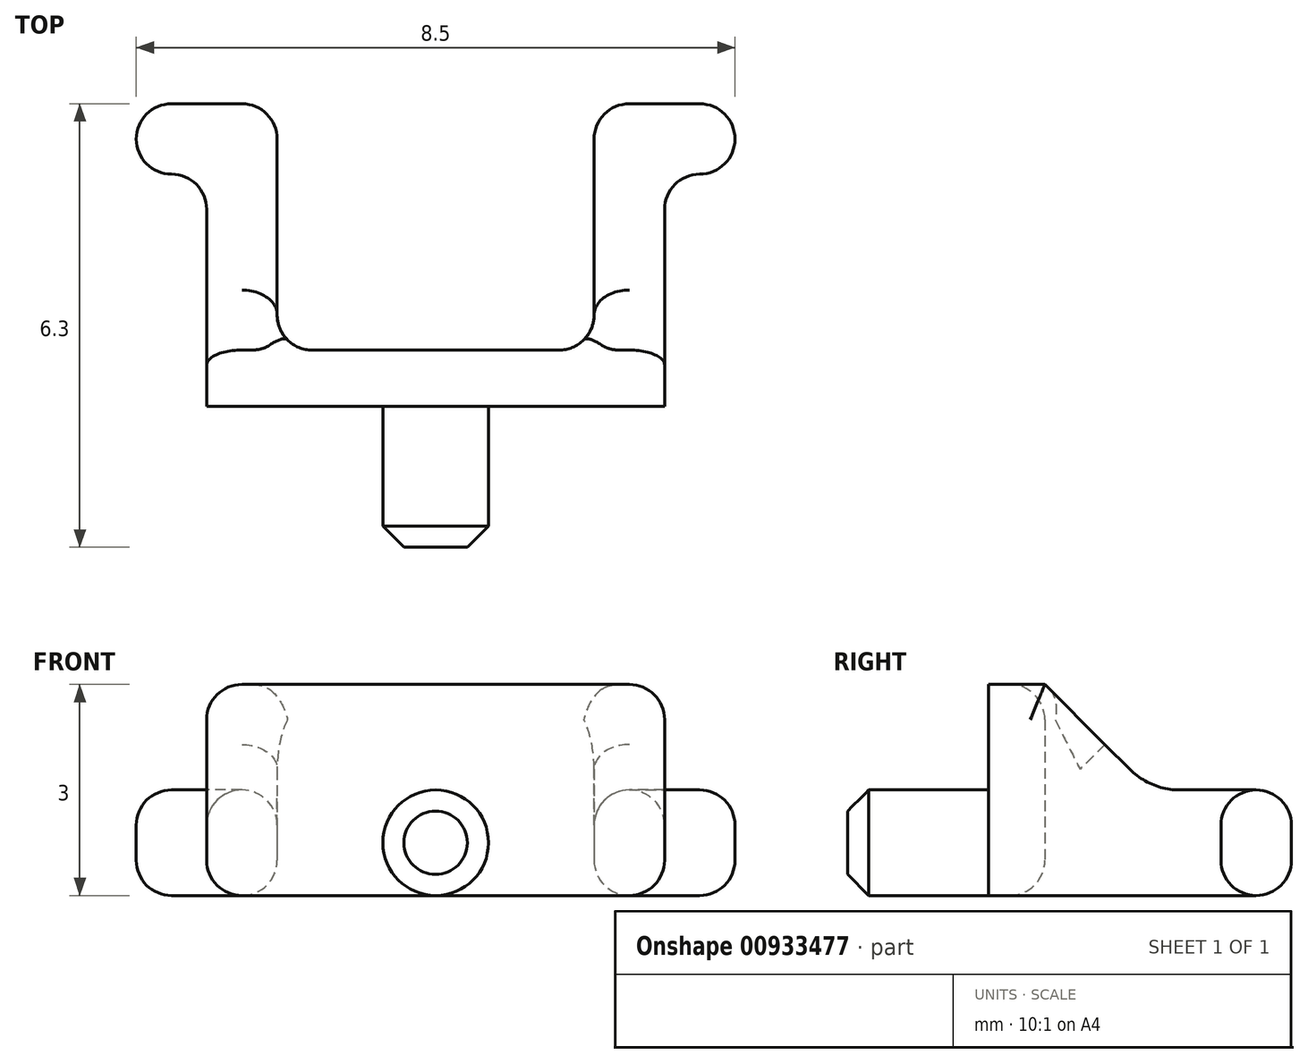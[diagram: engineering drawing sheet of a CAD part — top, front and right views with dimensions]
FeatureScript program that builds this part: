
annotation { "Feature Type Name" : "Feature", "Feature Type Description" : "" }
export const myFeature = defineFeature(function(context is Context, id is Id, definition is map)
    precondition{}
    {
        {
            var Q0;
            Q0=qCreatedBy(makeId("Top.planeOp"),FACE);
            var sketch = newSketch(context, id + "F0", { "sketchPlane" : qUnion([Q0])});
            skLineSegment(sketch, "E0", {"start": v(-3.25, 0) * mm, "end": v(-0.75, 0) * mm});
            skPoint(sketch, "E1", {"position": v(0, 0) * mm});
            skLineSegment(sketch, "E2", {"start": v(0, -3) * mm, "end": v(0, 7.11) * mm, "construction": true});
            skLineSegment(sketch, "E3", {"start": v(2.25, 1.3) * mm, "end": v(2.25, 3.8) * mm});
            skLineSegment(sketch, "E4", {"start": v(-2.25, 1.3) * mm, "end": v(-2.25, 3.8) * mm});
            skLineSegment(sketch, "E5", {"start": v(-1.75, 0.8) * mm, "end": v(1.75, 0.8) * mm});
            skPoint(sketch, "E6", {"position": v(0, 0.8) * mm});
            skLineSegment(sketch, "E7", {"start": v(-2.75, 4.3) * mm, "end": v(-3.75, 4.3) * mm});
            skLineSegment(sketch, "E8", {"start": v(2.75, 4.3) * mm, "end": v(3.75, 4.3) * mm});
            skLineSegment(sketch, "E9", {"start": v(-4.25, 3.8) * mm, "end": v(-4.25, 3.8) * mm});
            skLineSegment(sketch, "E10", {"start": v(-3.75, 3.3) * mm, "end": v(-3.75, 3.3) * mm});
            skLineSegment(sketch, "E11", {"start": v(-3.25, 2.8) * mm, "end": v(-3.25, 0) * mm});
            skLineSegment(sketch, "E12", {"start": v(4.25, 3.8) * mm, "end": v(4.25, 3.8) * mm});
            skLineSegment(sketch, "E13", {"start": v(3.75, 3.3) * mm, "end": v(3.75, 3.3) * mm});
            skLineSegment(sketch, "E14", {"start": v(3.25, 2.8) * mm, "end": v(3.25, 0) * mm});
            skPoint(sketch, "E15.visualSharp", {"position": v(-2.25, 0.8) * mm});
            skArc(sketch, "E15.filletArc", {"start": v(-2.25, 1.3) * mm, "mid": v(-2.1, 0.95) * mm, "end": v(-1.75, 0.8) * mm});
            skPoint(sketch, "E16.visualSharp", {"position": v(2.25, 0.8) * mm});
            skArc(sketch, "E16.filletArc", {"start": v(1.75, 0.8) * mm, "mid": v(2.1, 0.95) * mm, "end": v(2.25, 1.3) * mm});
            skPoint(sketch, "E17.visualSharp", {"position": v(3.25, 0.8) * mm});
            skPoint(sketch, "E18.visualSharp", {"position": v(3.25, 3.3) * mm});
            skArc(sketch, "E18.filletArc", {"start": v(3.75, 3.3) * mm, "mid": v(3.4, 3.15) * mm, "end": v(3.25, 2.8) * mm});
            skPoint(sketch, "E19.visualSharp", {"position": v(-3.25, 0.8) * mm});
            skPoint(sketch, "E20.visualSharp", {"position": v(-3.25, 3.3) * mm});
            skArc(sketch, "E20.filletArc", {"start": v(-3.25, 2.8) * mm, "mid": v(-3.4, 3.15) * mm, "end": v(-3.75, 3.3) * mm});
            skPoint(sketch, "E21.visualSharp", {"position": v(-2.25, 4.3) * mm});
            skArc(sketch, "E21.filletArc", {"start": v(-2.25, 3.8) * mm, "mid": v(-2.4, 4.15) * mm, "end": v(-2.75, 4.3) * mm});
            skPoint(sketch, "E22.visualSharp", {"position": v(2.25, 4.3) * mm});
            skArc(sketch, "E22.filletArc", {"start": v(2.75, 4.3) * mm, "mid": v(2.4, 4.15) * mm, "end": v(2.25, 3.8) * mm});
            skPoint(sketch, "E23.visualSharp", {"position": v(4.25, 4.3) * mm});
            skArc(sketch, "E23.filletArc", {"start": v(4.25, 3.8) * mm, "mid": v(4.1, 4.15) * mm, "end": v(3.75, 4.3) * mm});
            skPoint(sketch, "E24.visualSharp", {"position": v(4.25, 3.3) * mm});
            skArc(sketch, "E24.filletArc", {"start": v(3.75, 3.3) * mm, "mid": v(4.1, 3.45) * mm, "end": v(4.25, 3.8) * mm});
            skPoint(sketch, "E25.visualSharp", {"position": v(-4.25, 4.3) * mm});
            skArc(sketch, "E25.filletArc", {"start": v(-3.75, 4.3) * mm, "mid": v(-4.1, 4.15) * mm, "end": v(-4.25, 3.8) * mm});
            skPoint(sketch, "E26.visualSharp", {"position": v(-4.25, 3.3) * mm});
            skArc(sketch, "E26.filletArc", {"start": v(-4.25, 3.8) * mm, "mid": v(-4.1, 3.45) * mm, "end": v(-3.75, 3.3) * mm});
            skLineSegment(sketch, "E27.top", {"start": v(-0.75, -2) * mm, "end": v(0.75, -2) * mm});
            skLineSegment(sketch, "E27.left", {"start": v(-0.75, 0) * mm, "end": v(-0.75, -2) * mm});
            skLineSegment(sketch, "E27.right", {"start": v(0.75, 0) * mm, "end": v(0.75, -2) * mm});
            skPoint(sketch, "E28", {"position": v(0, -2) * mm});
            skLineSegment(sketch, "E29.trimOffspring", {"start": v(0.75, 0) * mm, "end": v(3.25, 0) * mm});
            skPoint(sketch, "E30.orphan", {"position": v(-5, 0) * mm});
            skPoint(sketch, "E31.orphan", {"position": v(5, 0) * mm});
            skSolve(sketch);
        }
        {
            var Q0;
            Q0=qSketchRegion(id+"F0",true);
            extrude(context, id + "F1", {"entities" : qUnion([Q0]), "depth" : 1.5 * mm, "offsetDistance" : 25 * mm});
        }
        {
            var Q0;
            Q0=makeQuery(id+"F1.opExtrude","CAP_FACE",FACE,{"disambiguationData":[OSD([sQuery(id+"F0.wireOp",EDGE,"E0"),sQuery(id+"F0.wireOp",EDGE,"6YUp3G7D-HScl-yHn5-GseC-h8JY3a3RTnfq"),sQuery(id+"F0.wireOp",EDGE,"Xoj59s7T-2QtX-ZDX5-LiLJ-oQHR1xyVejqm"),sQuery(id+"F0.wireOp",EDGE,"Zc0sCTJD-TUej-OjTx-Aevo-d0EqPVeEhSTX"),sQuery(id+"F0.wireOp",EDGE,"E3"),sQuery(id+"F0.wireOp",EDGE,"E4"),sQuery(id+"F0.wireOp",EDGE,"fb0ed693-0343-43f7-9de8-dc647e30bef6.trimOffspring"),sQuery(id+"F0.wireOp",EDGE,"E5"),sQuery(id+"F0.wireOp",EDGE,"E7"),sQuery(id+"F0.wireOp",EDGE,"E8"),sQuery(id+"F0.wireOp",EDGE,"E15.filletArc"),sQuery(id+"F0.wireOp",EDGE,"E16.filletArc"),sQuery(id+"F0.wireOp",EDGE,"E17.filletArc"),sQuery(id+"F0.wireOp",EDGE,"E18.filletArc"),sQuery(id+"F0.wireOp",EDGE,"E19.filletArc"),sQuery(id+"F0.wireOp",EDGE,"E20.filletArc"),sQuery(id+"F0.wireOp",EDGE,"E21.filletArc"),sQuery(id+"F0.wireOp",EDGE,"E22.filletArc"),sQuery(id+"F0.wireOp",EDGE,"E23.filletArc"),sQuery(id+"F0.wireOp",EDGE,"E24.filletArc"),sQuery(id+"F0.wireOp",EDGE,"E25.filletArc"),sQuery(id+"F0.wireOp",EDGE,"E26.filletArc")])],"isStart":false});
            var sketch = newSketch(context, id + "F2", { "sketchPlane" : qUnion([Q0])});
            skLineSegment(sketch, "E32.0", {"start": v(-3.25, 0) * mm, "end": v(-3.25, 0) * mm});
            skLineSegment(sketch, "E33.0", {"start": v(-3.25, 0) * mm, "end": v(-3.25, 0.8) * mm});
            skLineSegment(sketch, "E34.0", {"start": v(3.25, 0.8) * mm, "end": v(3.25, 0) * mm});
            skLineSegment(sketch, "E35", {"start": v(-3.25, 0.8) * mm, "end": v(3.25, 0.8) * mm});
            skLineSegment(sketch, "E36.0", {"start": v(-3.25, 0) * mm, "end": v(3.25, 0) * mm});
            skPoint(sketch, "E37.orphan", {"position": v(-0.75, 0) * mm});
            skSolve(sketch);
        }
        {
            var Q0;
            Q0=qSketchRegion(id+"F2",true);
            extrude(context, id + "F3", {"entities" : qUnion([Q0]), "operationType" : NewBodyOperationType.ADD, "depth" : 1.5 * mm, "offsetDistance" : 25 * mm});
        }
        {
            var Q0;
            {var subQ4=sQuery(id+"F0.wireOp",EDGE,"E15.filletArc");var subQ5=sQuery(id+"F2.wireOp",EDGE,"E35");Q0=makeQuery(id+"F3.boolean.opBoolean","SPLIT",EDGE,{"disambiguationData":[TD([makeQuery(id+"F1.opExtrude","SWEPT_FACE",FACE,{"disambiguationData":[OSD([subQ4])]})])],"derivedFrom":makeQuery(id+"F3.opExtrude","CAP_EDGE",EDGE,{"disambiguationData":[OSD([subQ5])],"isStart":true})});}
            var Q1;
            {var subQ3=sQuery(id+"F0.wireOp",EDGE,"E16.filletArc");var subQ5=sQuery(id+"F2.wireOp",EDGE,"E35");Q1=makeQuery(id+"F3.boolean.opBoolean","SPLIT",EDGE,{"disambiguationData":[TD([makeQuery(id+"F1.opExtrude","SWEPT_FACE",FACE,{"disambiguationData":[OSD([subQ3])]})])],"derivedFrom":makeQuery(id+"F3.opExtrude","CAP_EDGE",EDGE,{"disambiguationData":[OSD([subQ5])],"isStart":true})});}
            chamfer(context, id + "F4", {"entities" : qUnion([Q0, Q1]), "width" : 1.5 * mm, "tangentPropagation" : true});
        }
        {
            var Q0;
            {var subQ0=sQuery(id+"F2.wireOp",EDGE,"E35");var subQ1=makeQuery(id+"F3.opExtrude","SWEPT_FACE",FACE,{"disambiguationData":[OSD([subQ0])]});var subQ2=sQuery(id+"F0.wireOp",EDGE,"E5");var subQ3=makeQuery(id+"F1.opExtrude","SWEPT_FACE",FACE,{"disambiguationData":[OSD([subQ2])]});var subQ4=sQuery(id+"F0.wireOp",EDGE,"fb0ed693-0343-43f7-9de8-dc647e30bef6.trimOffspring");var subQ5=makeQuery(id+"F1.opExtrude","SWEPT_FACE",FACE,{"disambiguationData":[OSD([subQ4])]});var subQ6=sQuery(id+"F0.wireOp",EDGE,"Xoj59s7T-2QtX-ZDX5-LiLJ-oQHR1xyVejqm");var subQ7=makeQuery(id+"F1.opExtrude","SWEPT_FACE",FACE,{"disambiguationData":[OSD([subQ6])]});var subQ9=sQuery(id+"F0.wireOp",EDGE,"E15.filletArc");Q0=makeQuery(id+"F4.opChamfer","BLEND_EDGE",EDGE,{"blendedFrom":[makeQuery(id+"F3.boolean.opBoolean","SPLIT",EDGE,{"disambiguationData":[TD([makeQuery(id+"F1.opExtrude","SWEPT_FACE",FACE,{"disambiguationData":[OSD([subQ9])]})])],"derivedFrom":makeQuery(id+"F3.opExtrude","CAP_EDGE",EDGE,{"disambiguationData":[OSD([subQ0])],"isStart":true})}),makeQuery(id+"F3.boolean.opBoolean","MERGE",FACE,{"derivedFrom":[subQ7,subQ5,subQ3,subQ1]})],"blendedInto":[makeQuery(id+"F3.boolean.opBoolean","MERGE",FACE,{"derivedFrom":[subQ7,subQ5,subQ3,subQ1]})]});}
            var Q1;
            {var subQ0=sQuery(id+"F2.wireOp",EDGE,"E35");var subQ1=makeQuery(id+"F3.opExtrude","SWEPT_FACE",FACE,{"disambiguationData":[OSD([subQ0])]});var subQ2=sQuery(id+"F0.wireOp",EDGE,"E5");var subQ3=makeQuery(id+"F1.opExtrude","SWEPT_FACE",FACE,{"disambiguationData":[OSD([subQ2])]});var subQ4=sQuery(id+"F0.wireOp",EDGE,"fb0ed693-0343-43f7-9de8-dc647e30bef6.trimOffspring");var subQ5=makeQuery(id+"F1.opExtrude","SWEPT_FACE",FACE,{"disambiguationData":[OSD([subQ4])]});var subQ6=sQuery(id+"F0.wireOp",EDGE,"Xoj59s7T-2QtX-ZDX5-LiLJ-oQHR1xyVejqm");var subQ7=makeQuery(id+"F1.opExtrude","SWEPT_FACE",FACE,{"disambiguationData":[OSD([subQ6])]});var subQ8=sQuery(id+"F0.wireOp",EDGE,"E16.filletArc");Q1=makeQuery(id+"F4.opChamfer","BLEND_EDGE",EDGE,{"blendedFrom":[makeQuery(id+"F3.boolean.opBoolean","SPLIT",EDGE,{"disambiguationData":[TD([makeQuery(id+"F1.opExtrude","SWEPT_FACE",FACE,{"disambiguationData":[OSD([subQ8])]})])],"derivedFrom":makeQuery(id+"F3.opExtrude","CAP_EDGE",EDGE,{"disambiguationData":[OSD([subQ0])],"isStart":true})}),makeQuery(id+"F3.boolean.opBoolean","MERGE",FACE,{"derivedFrom":[subQ7,subQ5,subQ3,subQ1]})],"blendedInto":[makeQuery(id+"F3.boolean.opBoolean","MERGE",FACE,{"derivedFrom":[subQ7,subQ5,subQ3,subQ1]})]});}
            var Q2;
            {var subQ0=sQuery(id+"F0.wireOp",EDGE,"E22.filletArc");var subQ1=sQuery(id+"F0.wireOp",EDGE,"E17.filletArc");var subQ3=sQuery(id+"F0.wireOp",EDGE,"E14");var subQ4=sQuery(id+"F0.wireOp",EDGE,"E8");var subQ5=sQuery(id+"F0.wireOp",EDGE,"E16.filletArc");var subQ6=makeQuery(id+"F1.opExtrude","SWEPT_FACE",FACE,{"disambiguationData":[OSD([subQ5])]});var subQ7=sQuery(id+"F0.wireOp",EDGE,"Xoj59s7T-2QtX-ZDX5-LiLJ-oQHR1xyVejqm");var subQ9=sQuery(id+"F0.wireOp",EDGE,"E5");var subQ11=sQuery(id+"F2.wireOp",EDGE,"E35");var subQ13=sQuery(id+"F0.wireOp",EDGE,"E18.filletArc");var subQ14=sQuery(id+"F0.wireOp",EDGE,"E3");var subQ15=sQuery(id+"F0.wireOp",EDGE,"fb0ed693-0343-43f7-9de8-dc647e30bef6.trimOffspring");var subQ17=sQuery(id+"F0.wireOp",EDGE,"E24.filletArc");var subQ18=sQuery(id+"F0.wireOp",EDGE,"E23.filletArc");var subQ19=makeQuery(id+"F1.opExtrude","CAP_FACE",FACE,{"disambiguationData":[OSD([sQuery(id+"F0.wireOp",EDGE,"E0"),sQuery(id+"F0.wireOp",EDGE,"6YUp3G7D-HScl-yHn5-GseC-h8JY3a3RTnfq"),subQ7,sQuery(id+"F0.wireOp",EDGE,"Zc0sCTJD-TUej-OjTx-Aevo-d0EqPVeEhSTX"),subQ14,sQuery(id+"F0.wireOp",EDGE,"E4"),subQ15,subQ9,sQuery(id+"F0.wireOp",EDGE,"E7"),subQ4,sQuery(id+"F0.wireOp",EDGE,"E11"),subQ3,sQuery(id+"F0.wireOp",EDGE,"E15.filletArc"),subQ5,subQ1,subQ13,sQuery(id+"F0.wireOp",EDGE,"E19.filletArc"),sQuery(id+"F0.wireOp",EDGE,"E20.filletArc"),sQuery(id+"F0.wireOp",EDGE,"E21.filletArc"),subQ0,subQ18,subQ17,sQuery(id+"F0.wireOp",EDGE,"E25.filletArc"),sQuery(id+"F0.wireOp",EDGE,"E26.filletArc")])],"isStart":false});Q2=makeQuery(id+"F4.opChamfer","BLEND_EDGE",EDGE,{"blendedFrom":[makeQuery(id+"F3.boolean.opBoolean","SPLIT",EDGE,{"disambiguationData":[TD([subQ6])],"derivedFrom":makeQuery(id+"F3.opExtrude","CAP_EDGE",EDGE,{"disambiguationData":[OSD([subQ11])],"isStart":true})}),makeQuery(id+"F3.boolean.opBoolean","SPLIT",FACE,{"disambiguationData":[TD([makeQuery(id+"F1.opExtrude","SWEPT_FACE",FACE,{"disambiguationData":[OSD([subQ14])]})])],"derivedFrom":subQ19})],"blendedInto":[makeQuery(id+"F3.boolean.opBoolean","SPLIT",FACE,{"disambiguationData":[TD([makeQuery(id+"F1.opExtrude","SWEPT_FACE",FACE,{"disambiguationData":[OSD([subQ14])]})])],"derivedFrom":subQ19})]});}
            var Q3;
            {var subQ0=sQuery(id+"F0.wireOp",EDGE,"E15.filletArc");var subQ1=makeQuery(id+"F1.opExtrude","SWEPT_FACE",FACE,{"disambiguationData":[OSD([subQ0])]});var subQ2=sQuery(id+"F0.wireOp",EDGE,"E11");var subQ3=sQuery(id+"F0.wireOp",EDGE,"E7");var subQ4=sQuery(id+"F0.wireOp",EDGE,"Xoj59s7T-2QtX-ZDX5-LiLJ-oQHR1xyVejqm");var subQ6=sQuery(id+"F0.wireOp",EDGE,"E21.filletArc");var subQ7=sQuery(id+"F0.wireOp",EDGE,"E5");var subQ9=sQuery(id+"F2.wireOp",EDGE,"E35");var subQ11=sQuery(id+"F0.wireOp",EDGE,"E19.filletArc");var subQ13=sQuery(id+"F0.wireOp",EDGE,"E4");var subQ14=sQuery(id+"F0.wireOp",EDGE,"E20.filletArc");var subQ15=sQuery(id+"F0.wireOp",EDGE,"fb0ed693-0343-43f7-9de8-dc647e30bef6.trimOffspring");var subQ17=sQuery(id+"F0.wireOp",EDGE,"E26.filletArc");var subQ18=sQuery(id+"F0.wireOp",EDGE,"E25.filletArc");var subQ19=makeQuery(id+"F1.opExtrude","CAP_FACE",FACE,{"disambiguationData":[OSD([sQuery(id+"F0.wireOp",EDGE,"E0"),sQuery(id+"F0.wireOp",EDGE,"6YUp3G7D-HScl-yHn5-GseC-h8JY3a3RTnfq"),subQ4,sQuery(id+"F0.wireOp",EDGE,"Zc0sCTJD-TUej-OjTx-Aevo-d0EqPVeEhSTX"),sQuery(id+"F0.wireOp",EDGE,"E3"),subQ13,subQ15,subQ7,subQ3,sQuery(id+"F0.wireOp",EDGE,"E8"),subQ2,sQuery(id+"F0.wireOp",EDGE,"E14"),subQ0,sQuery(id+"F0.wireOp",EDGE,"E16.filletArc"),sQuery(id+"F0.wireOp",EDGE,"E17.filletArc"),sQuery(id+"F0.wireOp",EDGE,"E18.filletArc"),subQ11,subQ14,subQ6,sQuery(id+"F0.wireOp",EDGE,"E22.filletArc"),sQuery(id+"F0.wireOp",EDGE,"E23.filletArc"),sQuery(id+"F0.wireOp",EDGE,"E24.filletArc"),subQ18,subQ17])],"isStart":false});Q3=makeQuery(id+"F4.opChamfer","BLEND_EDGE",EDGE,{"blendedFrom":[makeQuery(id+"F3.boolean.opBoolean","SPLIT",EDGE,{"disambiguationData":[TD([subQ1])],"derivedFrom":makeQuery(id+"F3.opExtrude","CAP_EDGE",EDGE,{"disambiguationData":[OSD([subQ9])],"isStart":true})}),makeQuery(id+"F3.boolean.opBoolean","SPLIT",FACE,{"disambiguationData":[TD([makeQuery(id+"F1.opExtrude","SWEPT_FACE",FACE,{"disambiguationData":[OSD([subQ13])]})])],"derivedFrom":subQ19})],"blendedInto":[makeQuery(id+"F3.boolean.opBoolean","SPLIT",FACE,{"disambiguationData":[TD([makeQuery(id+"F1.opExtrude","SWEPT_FACE",FACE,{"disambiguationData":[OSD([subQ13])]})])],"derivedFrom":subQ19})]});}
            fillet(context, id + "F5", {"entities" : qUnion([Q0, Q1, Q2, Q3]), "radius" : 1 * mm, "tangentPropagation" : true, "allowEdgeOverflow" : false});
        }
        {
            var Q0;
            Q0=makeQuery(id+"F3.opExtrude","CAP_EDGE",EDGE,{"disambiguationData":[OSD([sQuery(id+"F2.wireOp",EDGE,"E35")])],"isStart":false});
            var Q1;
            Q1=makeQuery(id+"F1.opExtrude","CAP_EDGE",EDGE,{"disambiguationData":[OSD([sQuery(id+"F0.wireOp",EDGE,"E8")])],"isStart":false});
            var Q2;
            Q2=makeQuery(id+"F1.opExtrude","CAP_EDGE",EDGE,{"disambiguationData":[OSD([sQuery(id+"F0.wireOp",EDGE,"E7")])],"isStart":false});
            var Q3;
            Q3=makeQuery(id+"F3.opExtrude","CAP_EDGE",EDGE,{"disambiguationData":[OSD([sQuery(id+"F2.wireOp",EDGE,"E34.0")])],"isStart":false});
            var Q4;
            Q4=makeQuery(id+"F3.opExtrude","CAP_EDGE",EDGE,{"disambiguationData":[OSD([sQuery(id+"F2.wireOp",EDGE,"E33.0")])],"isStart":false});
            var Q5;
            Q5=makeQuery(id+"F1.opExtrude","CAP_EDGE",EDGE,{"disambiguationData":[OSD([sQuery(id+"F0.wireOp",EDGE,"E5")])],"isStart":true});
            fillet(context, id + "F6", {"entities" : qUnion([Q0, Q1, Q2, Q3, Q4, Q5]), "radius" : 0.5 * mm, "tangentPropagation" : true, "defaultsChanged" : false, "vertexSettings" : [], "allowEdgeOverflow" : false});
        }
        {
            var Q0;
            Q0=makeQuery(id+"F1.opExtrude","CAP_EDGE",EDGE,{"disambiguationData":[OSD([sQuery(id+"F0.wireOp",EDGE,"E27.left")])],"isStart":false});
            var Q1;
            Q1=makeQuery(id+"F1.opExtrude","CAP_EDGE",EDGE,{"disambiguationData":[OSD([sQuery(id+"F0.wireOp",EDGE,"E27.right")])],"isStart":false});
            var Q2;
            Q2=makeQuery(id+"F1.opExtrude","CAP_EDGE",EDGE,{"disambiguationData":[OSD([sQuery(id+"F0.wireOp",EDGE,"E27.right")])],"isStart":true});
            var Q3;
            Q3=makeQuery(id+"F1.opExtrude","CAP_EDGE",EDGE,{"disambiguationData":[OSD([sQuery(id+"F0.wireOp",EDGE,"E27.left")])],"isStart":true});
            fillet(context, id + "F7", {"entities" : qUnion([Q0, Q1, Q2, Q3]), "tangentPropagation" : true, "radius" : 0.75 * mm, "defaultsChanged" : false, "vertexSettings" : [], "allowEdgeOverflow" : false});
        }
        {
            var Q0;
            Q0=makeQuery(id+"F7.opFillet","BLEND_EDGE",EDGE,{"blendedFrom":[makeQuery(id+"F1.opExtrude","CAP_EDGE",EDGE,{"disambiguationData":[OSD([sQuery(id+"F0.wireOp",EDGE,"E27.left")])],"isStart":true}),makeQuery(id+"F1.opExtrude","SWEPT_FACE",FACE,{"disambiguationData":[OSD([sQuery(id+"F0.wireOp",EDGE,"E27.top")])]})],"blendedInto":[makeQuery(id+"F1.opExtrude","SWEPT_FACE",FACE,{"disambiguationData":[OSD([sQuery(id+"F0.wireOp",EDGE,"E27.top")])]})]});
            chamfer(context, id + "F8", {"entities" : qUnion([Q0]), "width" : 0.3 * mm, "tangentPropagation" : true});
        }
    });
